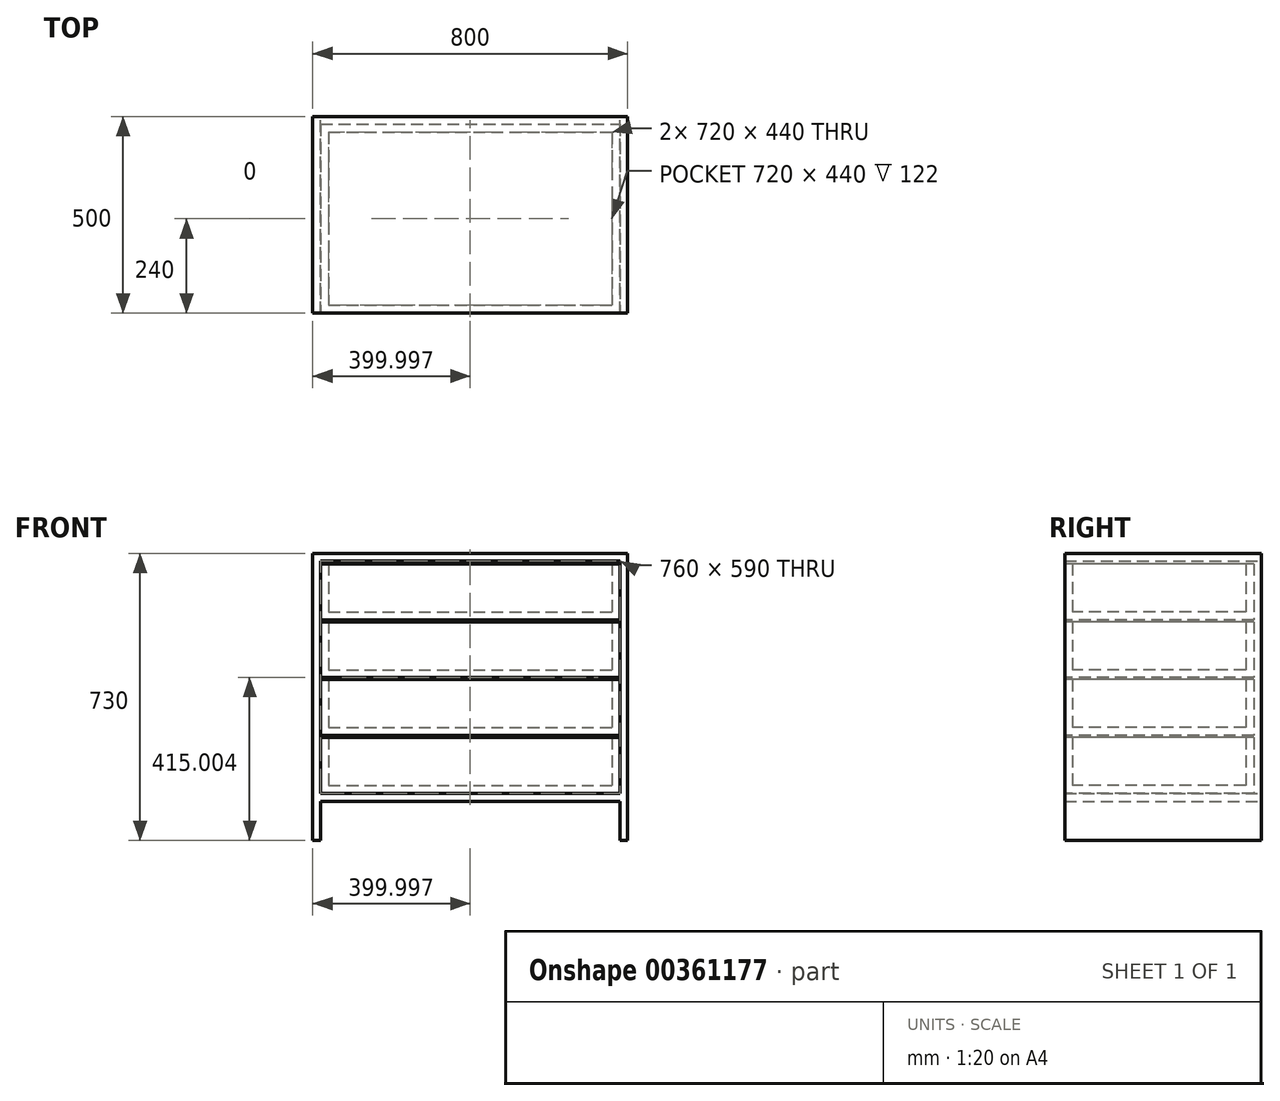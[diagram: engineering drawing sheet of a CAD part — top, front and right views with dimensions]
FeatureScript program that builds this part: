
annotation { "Feature Type Name" : "Feature", "Feature Type Description" : "" }
export const myFeature = defineFeature(function(context is Context, id is Id, definition is map)
    precondition{}
    {
        {
            var Q0;
            Q0=qCreatedBy(makeId("Front.planeOp"),FACE);
            var sketch = newSketch(context, id + "F0", { "sketchPlane" : qUnion([Q0])});
            skLineSegment(sketch, "E0", {"start": v(-301.72, 332.62) * mm, "end": v(-301.72, -377.38) * mm});
            skLineSegment(sketch, "E1", {"start": v(-301.72, -377.38) * mm, "end": v(-281.72, -377.38) * mm});
            skLineSegment(sketch, "E2.0", {"start": v(-281.72, 332.62) * mm, "end": v(-281.72, -377.38) * mm});
            skLineSegment(sketch, "E3", {"start": v(-301.72, 332.62) * mm, "end": v(-281.72, 332.62) * mm});
            skLineSegment(sketch, "E4", {"start": v(478.28, 332.62) * mm, "end": v(478.28, -377.38) * mm});
            skLineSegment(sketch, "E5", {"start": v(478.28, -377.38) * mm, "end": v(498.28, -377.38) * mm});
            skLineSegment(sketch, "E6.0", {"start": v(498.28, 332.62) * mm, "end": v(498.28, -377.38) * mm});
            skLineSegment(sketch, "E7", {"start": v(478.28, 332.62) * mm, "end": v(498.28, 332.62) * mm});
            skLineSegment(sketch, "E8", {"start": v(-301.72, 332.62) * mm, "end": v(-301.72, 352.62) * mm});
            skLineSegment(sketch, "E9", {"start": v(-301.72, 352.62) * mm, "end": v(498.28, 352.62) * mm});
            skLineSegment(sketch, "E10", {"start": v(498.28, 352.62) * mm, "end": v(498.28, 332.62) * mm});
            skLineSegment(sketch, "E11", {"start": v(-301.72, 332.62) * mm, "end": v(498.28, 332.62) * mm});
            skLineSegment(sketch, "E12", {"start": v(478.28, -377.38) * mm, "end": v(478.28, -277.38) * mm});
            skLineSegment(sketch, "E13", {"start": v(478.28, -277.38) * mm, "end": v(-281.72, -277.38) * mm});
            skLineSegment(sketch, "E14", {"start": v(-281.72, -277.38) * mm, "end": v(-281.72, -257.38) * mm});
            skLineSegment(sketch, "E15", {"start": v(-281.72, -257.38) * mm, "end": v(478.28, -257.38) * mm});
            skLineSegment(sketch, "E16", {"start": v(478.28, -257.38) * mm, "end": v(478.28, -277.38) * mm});
            skSolve(sketch);
        }
        {
            var Q0;
            {var subQ1=sQuery(id+"F0.wireOp",EDGE,"E8");Q0=makeQuery(id+"F0.imprint","IMPRINT",FACE,{"disambiguationData":[TD([[makeQuery(id+"F0.imprint","IMPRINT",EDGE,{"derivedFrom":subQ1}),-1.0]])]});}
            var Q1;
            {var subQ5=sQuery(id+"F0.wireOp",EDGE,"E0");Q1=makeQuery(id+"F0.imprint","IMPRINT",FACE,{"disambiguationData":[TD([[makeQuery(id+"F0.imprint","IMPRINT",EDGE,{"derivedFrom":subQ5}),1.0]])]});}
            var Q2;
            Q2=makeQuery(id+"F0.imprint","IMPRINT",FACE,{"disambiguationData":[TD([[makeQuery(id+"F0.imprint","IMPRINT",EDGE,{"derivedFrom":sQuery(id+"F0.wireOp",EDGE,"E13")}),-1.0]])]});
            var Q3;
            {var subQ1=sQuery(id+"F0.wireOp",EDGE,"E4");Q3=makeQuery(id+"F0.imprint","IMPRINT",FACE,{"disambiguationData":[TD([[makeQuery(id+"F0.imprint","IMPRINT",EDGE,{"derivedFrom":subQ1}),1.0]])]});}
            extrude(context, id + "F1", {"entities" : qUnion([Q0, Q1, Q2, Q3]), "depth" : 500 * mm});
        }
        {
            var Q0;
            Q0=makeQuery(id+"F1.opExtrude","CAP_FACE",FACE,{"disambiguationData":[OSD([sQuery(id+"F0.wireOp",EDGE,"E0"),sQuery(id+"F0.wireOp",EDGE,"E1"),sQuery(id+"F0.wireOp",EDGE,"E2.0"),sQuery(id+"F0.wireOp",EDGE,"E4"),sQuery(id+"F0.wireOp",EDGE,"E5"),sQuery(id+"F0.wireOp",EDGE,"E6.0"),sQuery(id+"F0.wireOp",EDGE,"E8"),sQuery(id+"F0.wireOp",EDGE,"E9"),sQuery(id+"F0.wireOp",EDGE,"E10"),sQuery(id+"F0.wireOp",EDGE,"E11"),sQuery(id+"F0.wireOp",EDGE,"E12"),sQuery(id+"F0.wireOp",EDGE,"E13"),sQuery(id+"F0.wireOp",EDGE,"E15")])],"isStart":false});
            var sketch = newSketch(context, id + "F2", { "sketchPlane" : qUnion([Q0])});
            skLineSegment(sketch, "E17.bottom", {"start": v(-281.72, -115.38) * mm, "end": v(478.28, -115.38) * mm});
            skLineSegment(sketch, "E17.top", {"start": v(-281.72, -257.38) * mm, "end": v(478.28, -257.38) * mm});
            skLineSegment(sketch, "E17.left", {"start": v(-281.72, -115.38) * mm, "end": v(-281.72, -257.38) * mm});
            skLineSegment(sketch, "E17.right", {"start": v(478.28, -115.38) * mm, "end": v(478.28, -257.38) * mm});
            skLineSegment(sketch, "E18.0", {"start": v(-281.72, -110.38) * mm, "end": v(478.28, -110.38) * mm});
            skLineSegment(sketch, "E19.0", {"start": v(-281.72, 31.62) * mm, "end": v(478.28, 31.62) * mm});
            skLineSegment(sketch, "E20.0", {"start": v(-281.72, 36.62) * mm, "end": v(478.28, 36.62) * mm});
            skLineSegment(sketch, "E21.0", {"start": v(-281.72, 178.62) * mm, "end": v(478.28, 178.62) * mm});
            skLineSegment(sketch, "E22.0", {"start": v(-281.72, 183.62) * mm, "end": v(478.28, 183.62) * mm});
            skLineSegment(sketch, "E23.0", {"start": v(-281.72, 325.62) * mm, "end": v(478.28, 325.62) * mm});
            skLineSegment(sketch, "E24", {"start": v(478.28, 325.62) * mm, "end": v(478.28, 183.62) * mm});
            skLineSegment(sketch, "E25", {"start": v(478.28, 178.62) * mm, "end": v(478.28, 36.62) * mm});
            skLineSegment(sketch, "E26", {"start": v(478.28, 31.62) * mm, "end": v(478.28, -110.38) * mm});
            skLineSegment(sketch, "E27", {"start": v(-281.72, 332.62) * mm, "end": v(-281.72, 183.62) * mm});
            skLineSegment(sketch, "E28", {"start": v(-281.72, 178.62) * mm, "end": v(-281.72, 36.62) * mm});
            skLineSegment(sketch, "E29", {"start": v(-281.72, 31.62) * mm, "end": v(-281.72, -110.38) * mm});
            skSolve(sketch);
        }
        {
            var Q0;
            Q0=makeQuery(id+"F2.imprint","IMPRINT",FACE,{"disambiguationData":[TD([[makeQuery(id+"F2.imprint","IMPRINT",EDGE,{"derivedFrom":sQuery(id+"F2.wireOp",EDGE,"E17.bottom")}),-1.0]])]});
            var Q1;
            Q1=makeQuery(id+"F2.imprint","IMPRINT",FACE,{"disambiguationData":[TD([[makeQuery(id+"F2.imprint","IMPRINT",EDGE,{"derivedFrom":sQuery(id+"F2.wireOp",EDGE,"E18.0")}),1.0]])]});
            var Q2;
            Q2=makeQuery(id+"F2.imprint","IMPRINT",FACE,{"disambiguationData":[TD([[makeQuery(id+"F2.imprint","IMPRINT",EDGE,{"derivedFrom":sQuery(id+"F2.wireOp",EDGE,"E20.0")}),1.0]])]});
            var Q3;
            {var subQ0=sQuery(id+"F2.wireOp",EDGE,"E22.0");Q3=makeQuery(id+"F2.imprint","IMPRINT",FACE,{"disambiguationData":[TD([[makeQuery(id+"F2.imprint","IMPRINT",EDGE,{"derivedFrom":subQ0}),1.0]])]});}
            extrude(context, id + "F3", {"entities" : qUnion([Q0, Q1, Q2, Q3]), "oppositeDirection" : true, "depth" : 480 * mm});
        }
        {
            var Q0;
            Q0=makeQuery(id+"F3.opExtrude","SWEPT_FACE",FACE,{"disambiguationData":[OSD([sQuery(id+"F2.wireOp",EDGE,"E23.0")])]});
            var Q1;
            Q1=makeQuery(id+"F3.opExtrude","SWEPT_FACE",FACE,{"disambiguationData":[OSD([sQuery(id+"F2.wireOp",EDGE,"E21.0")])]});
            var Q2;
            Q2=makeQuery(id+"F3.opExtrude","SWEPT_FACE",FACE,{"disambiguationData":[OSD([sQuery(id+"F2.wireOp",EDGE,"E19.0")])]});
            var Q3;
            Q3=makeQuery(id+"F3.opExtrude","SWEPT_FACE",FACE,{"disambiguationData":[OSD([sQuery(id+"F2.wireOp",EDGE,"E17.bottom")])]});
            shell(context, id + "F4", {"entities" : qUnion([Q0, Q1, Q2, Q3]), "thickness" : 20 * mm});
        }
    });
